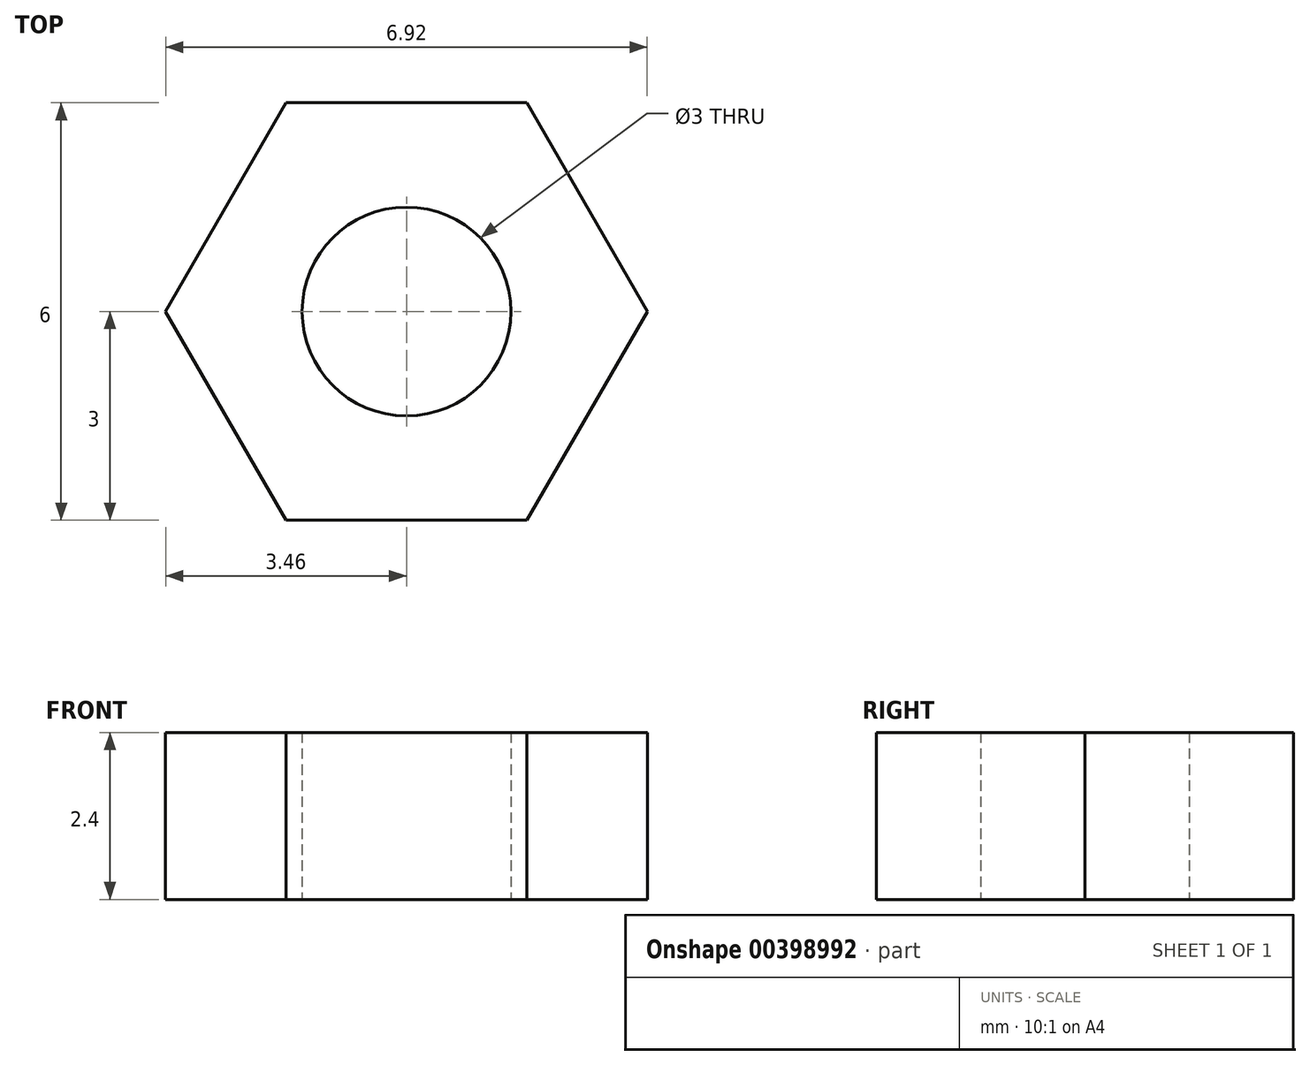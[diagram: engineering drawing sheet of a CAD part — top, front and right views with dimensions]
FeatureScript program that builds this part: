
annotation { "Feature Type Name" : "Feature", "Feature Type Description" : "" }
export const myFeature = defineFeature(function(context is Context, id is Id, definition is map)
    precondition{}
    {
        {
            var Q0;
            Q0=qCreatedBy(makeId("Top.planeOp"),FACE);
            var sketch = newSketch(context, id + "F0", { "sketchPlane" : qUnion([Q0])});
            skCircle(sketch, "E0.cCircle", {"center": v(0, 0) * mm, "radius": 3 * mm, "construction": true});
            skLineSegment(sketch, "E0.0", {"start": v(1.73, -3) * mm, "end": v(-1.73, -3) * mm});
            skLineSegment(sketch, "E0.1", {"start": v(-1.73, -3) * mm, "end": v(-3.46, 0) * mm});
            skLineSegment(sketch, "E0.2", {"start": v(-3.46, 0) * mm, "end": v(-1.73, 3) * mm});
            skLineSegment(sketch, "E0.3", {"start": v(-1.73, 3) * mm, "end": v(1.73, 3) * mm});
            skLineSegment(sketch, "E0.4", {"start": v(1.73, 3) * mm, "end": v(3.46, 0) * mm});
            skLineSegment(sketch, "E0.5", {"start": v(3.46, 0) * mm, "end": v(1.73, -3) * mm});
            skPoint(sketch, "E0.0.midPoint", {"position": v(0, -3) * mm});
            skCircle(sketch, "E1", {"center": v(0, 0) * mm, "radius": 1.5 * mm});
            skSolve(sketch);
        }
        {
            var Q0;
            Q0=qSketchRegion(id+"F0",true);
            extrude(context, id + "F1", {"entities" : qUnion([Q0]), "depth" : 2.4 * mm});
        }
    });
